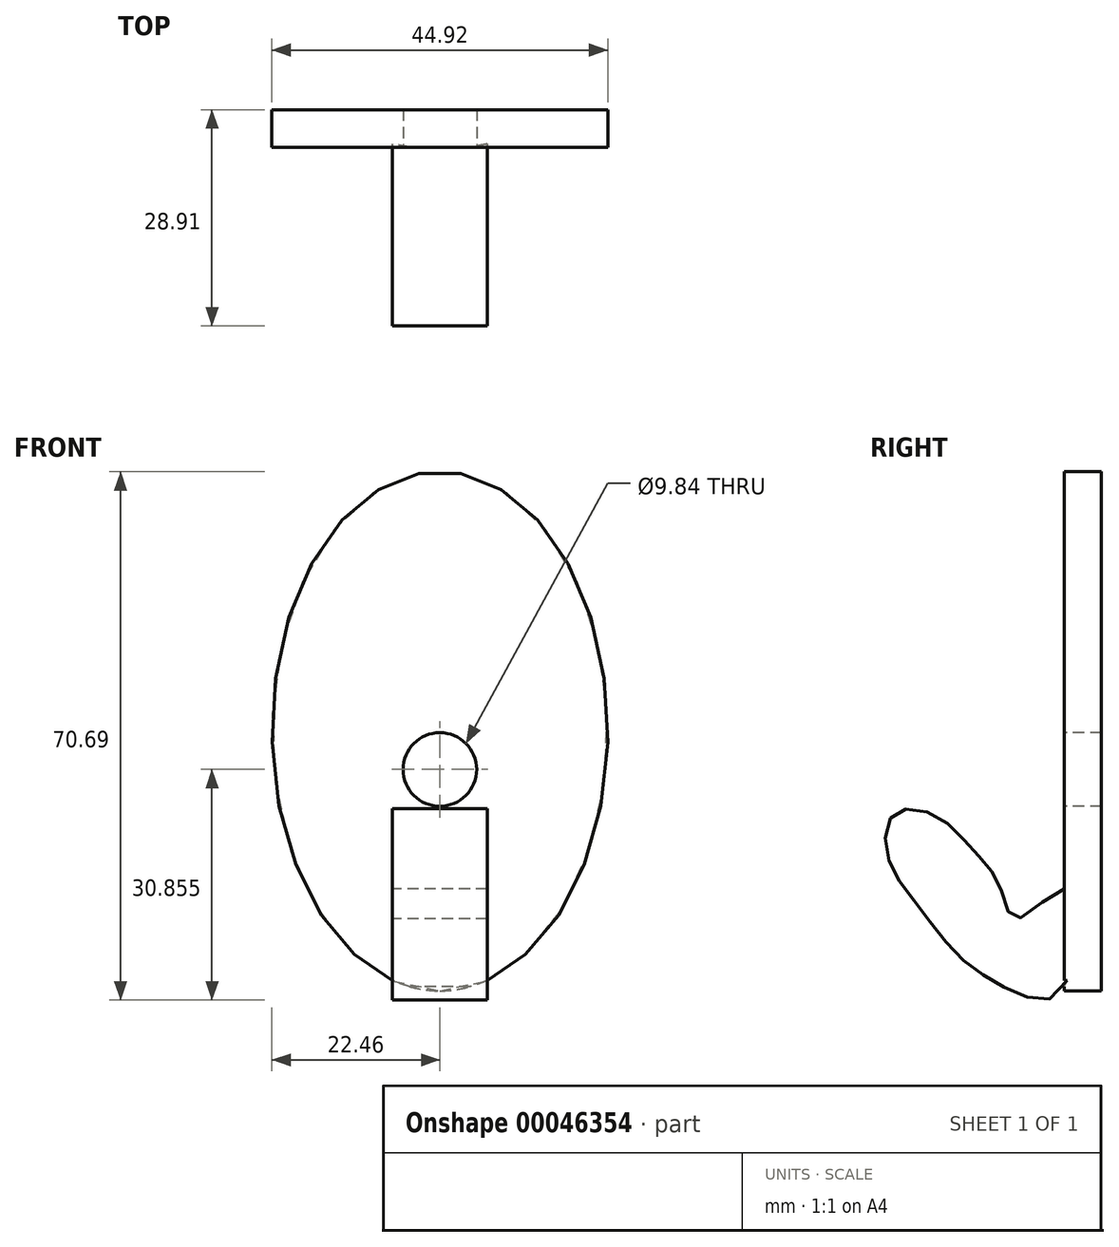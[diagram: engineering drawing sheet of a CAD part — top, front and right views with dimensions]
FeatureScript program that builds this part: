
annotation { "Feature Type Name" : "Feature", "Feature Type Description" : "" }
export const myFeature = defineFeature(function(context is Context, id is Id, definition is map)
    precondition{}
    {
        {
            var Q0;
            Q0=qCreatedBy(makeId("Front.planeOp"),FACE);
            var sketch = newSketch(context, id + "F0", { "sketchPlane" : qUnion([Q0])});
            skEllipse(sketch, "E0", {"center": v(0, 34.72) * mm, "majorRadius": 34.72 * mm, "minorRadius": 22.46 * mm, "majorAxis": v(0, -1)});
            skSolve(sketch);
        }
        {
            var Q0;
            Q0=makeQuery(id+"F0.imprint","IMPRINT",FACE,{"disambiguationData":[TD([[makeQuery(id+"F0.imprint","IMPRINT",EDGE,{"derivedFrom":sQuery(id+"F0.wireOp",EDGE,"E0")}),1.0]])]});
            extrude(context, id + "F1", {"entities" : qUnion([Q0]), "depth" : 5 * mm});
        }
        {
            var Q0;
            Q0=makeQuery(id+"F1.opExtrude","CAP_FACE",FACE,{"disambiguationData":[OSD([sQuery(id+"F0.wireOp",EDGE,"E0")])],"isStart":false});
            var sketch = newSketch(context, id + "F2", { "sketchPlane" : qUnion([Q0])});
            skCircle(sketch, "E1", {"center": v(0, 29.62) * mm, "radius": 4.92 * mm});
            skSolve(sketch);
        }
        {
            var Q0;
            Q0=makeQuery(id+"F2.imprint","IMPRINT",FACE,{"disambiguationData":[TD([[makeQuery(id+"F2.imprint","IMPRINT",EDGE,{"derivedFrom":sQuery(id+"F2.wireOp",EDGE,"E1")}),1.0]])]});
            extrude(context, id + "F3", {"entities" : qUnion([Q0]), "operationType" : NewBodyOperationType.REMOVE, "oppositeDirection" : true, "depth" : 28.25 * mm});
        }
        {
            var Q0;
            Q0=qCreatedBy(makeId("Right.planeOp"),FACE);
            var sketch = newSketch(context, id + "F4", { "sketchPlane" : qUnion([Q0])});
            skFitSpline(sketch, "E2", {"points": [v(-5.4, 0) * mm, v(-11.94, 0) * mm, v(-18.82, 4.42) * mm, v(-24.7, 11.62) * mm, v(-28.63, 18.16) * mm, v(-27.65, 23.72) * mm, v(-22.09, 23.4) * mm, v(-16.85, 18.49) * mm, v(-13.58, 13.9) * mm, v(-11.29, 9.65) * mm, v(-4.42, 13.58) * mm, v(-5.4, 0) * mm]});
            skSolve(sketch);
        }
        {
            var Q0;
            Q0=makeQuery(id+"F4.imprint","IMPRINT",FACE,{"disambiguationData":[TD([[makeQuery(id+"F4.imprint","IMPRINT",EDGE,{"derivedFrom":sQuery(id+"F4.wireOp",EDGE,"E2")}),-1.0]])]});
            extrude(context, id + "F5", {"entities" : qUnion([Q0]), "operationType" : NewBodyOperationType.ADD, "endBound" : BoundingType.SYMMETRIC, "depth" : 12.7 * mm});
        }
    });
